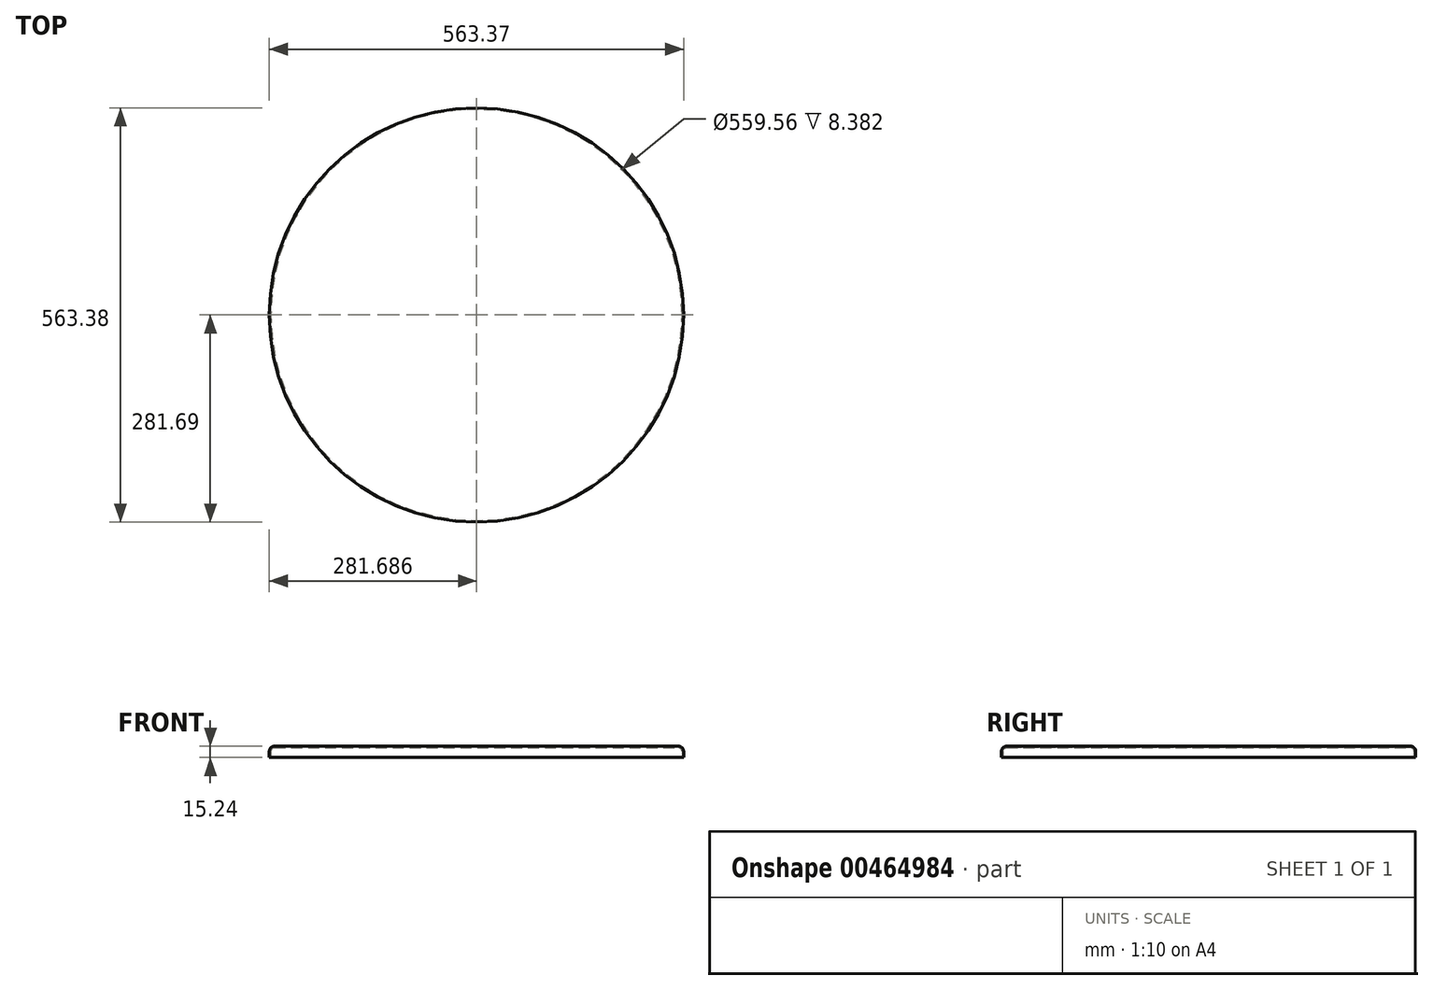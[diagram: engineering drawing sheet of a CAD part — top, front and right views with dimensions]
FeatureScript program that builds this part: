
annotation { "Feature Type Name" : "Feature", "Feature Type Description" : "" }
export const myFeature = defineFeature(function(context is Context, id is Id, definition is map)
    precondition{}
    {
        {
            var Q0;
            Q0=qCreatedBy(makeId("Front.planeOp"),FACE);
            var sketch = newSketch(context, id + "F0", { "sketchPlane" : qUnion([Q0])});
            skLineSegment(sketch, "E0", {"start": v(0, 0) * mm, "end": v(0, 8.38) * mm});
            skLineSegment(sketch, "E1", {"start": v(6.86, 15.24) * mm, "end": v(23.5, 15.24) * mm});
            skPoint(sketch, "E2.visualSharp", {"position": v(0, 15.24) * mm});
            skArc(sketch, "E2.filletArc", {"start": v(6.86, 15.24) * mm, "mid": v(2, 13.23) * mm, "end": v(0, 8.38) * mm});
            skLineSegment(sketch, "E3", {"start": v(6.86, 15.24) * mm, "end": v(281.69, 15.24) * mm});
            skLineSegment(sketch, "E4.0", {"start": v(6.86, 13.33) * mm, "end": v(281.69, 13.33) * mm});
            skArc(sketch, "E4.1", {"start": v(6.86, 13.33) * mm, "mid": v(3.36, 11.88) * mm, "end": v(1.9, 8.38) * mm});
            skLineSegment(sketch, "E4.2", {"start": v(1.9, 0) * mm, "end": v(1.9, 8.38) * mm});
            skLineSegment(sketch, "E5", {"start": v(1.9, 0) * mm, "end": v(0, 0) * mm});
            skLineSegment(sketch, "E6", {"start": v(281.69, 13.33) * mm, "end": v(281.69, 15.24) * mm});
            skSolve(sketch);
        }
        {
            var Q0;
            Q0=makeQuery(id+"F0.imprint","IMPRINT",FACE,{"disambiguationData":[TD([[makeQuery(id+"F0.imprint","IMPRINT",EDGE,{"derivedFrom":sQuery(id+"F0.wireOp",EDGE,"E0")}),-1.0]])]});
            var Q1;
            Q1=sQuery(id+"F0.wireOp",EDGE,"E6");
            revolve(context, id + "F1", {"entities" : qUnion([Q0]), "axis" : qUnion([Q1]), "revolveType" : RevolveType.FULL});
        }
    });
